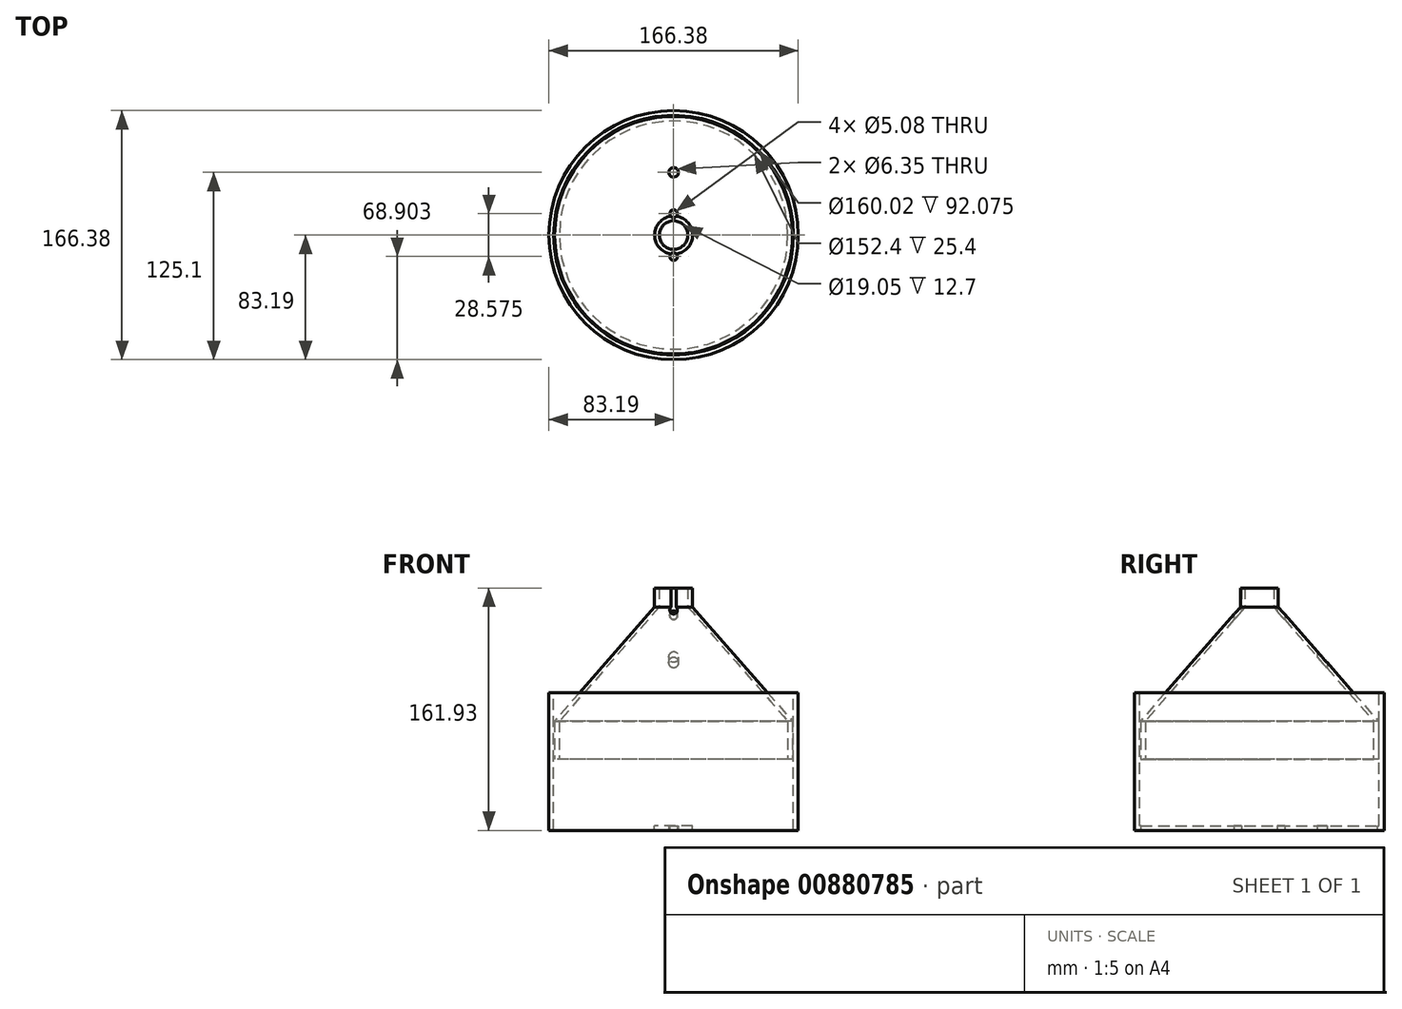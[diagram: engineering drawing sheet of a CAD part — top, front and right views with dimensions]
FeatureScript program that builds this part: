
annotation { "Feature Type Name" : "Feature", "Feature Type Description" : "" }
export const myFeature = defineFeature(function(context is Context, id is Id, definition is map)
    precondition{}
    {
        {
            var Q0;
            Q0=qCreatedBy(makeId("Top.planeOp"),FACE);
            var sketch = newSketch(context, id + "F0", { "sketchPlane" : qUnion([Q0])});
            skCircle(sketch, "E0", {"center": v(0, 0) * mm, "radius": 76.2 * mm});
            skCircle(sketch, "E1", {"center": v(0, 0) * mm, "radius": 79.38 * mm});
            skSolve(sketch);
        }
        {
            var Q0;
            Q0=makeQuery(id+"F0.imprint","IMPRINT",FACE,{"disambiguationData":[TD([[makeQuery(id+"F0.imprint","IMPRINT",EDGE,{"derivedFrom":sQuery(id+"F0.wireOp",EDGE,"E0")}),-1.0]])]});
            extrude(context, id + "F1", {"entities" : qUnion([Q0]), "depth" : 25.4 * mm, "offsetDistance" : 25.4 * mm});
        }
        {
            var Q0;
            Q0=qCreatedBy(makeId("Top.planeOp"),FACE);
            cPlane(context, id + "F2", {"entities" : qUnion([Q0]), "cplaneType" : CPlaneType.OFFSET, "offset" : 101.6 * mm, "width" : 152.4 * mm, "height" : 152.4 * mm});
        }
        {
            var Q0;
            Q0=qCreatedBy(id+"F2.planeOp",FACE);
            var sketch = newSketch(context, id + "F3", { "sketchPlane" : qUnion([Q0])});
            skCircle(sketch, "E2", {"center": v(0, 0) * mm, "radius": 12.7 * mm});
            skCircle(sketch, "E3", {"center": v(0, 0) * mm, "radius": 9.53 * mm, "construction": true});
            skSolve(sketch);
        }
        {
            var Q0;
            Q0=makeQuery(id+"F1.opExtrude","CAP_FACE",FACE,{"disambiguationData":[OSD([sQuery(id+"F0.wireOp",EDGE,"E0"),sQuery(id+"F0.wireOp",EDGE,"E1")])],"isStart":false});
            var sketch = newSketch(context, id + "F4", { "sketchPlane" : qUnion([Q0])});
            skCircle(sketch, "E4.0", {"center": v(0, 0) * mm, "radius": 79.38 * mm});
            skSolve(sketch);
        }
        {
            var Q1;
            Q1 = qSketchRegion(id + "F4", true);
            var Q2;
            Q2=makeQuery(id+"F3.imprint","IMPRINT",FACE,{"disambiguationData":[TD([[makeQuery(id+"F3.imprint","IMPRINT",EDGE,{"derivedFrom":sQuery(id+"F3.wireOp",EDGE,"E2")}),1.0]])]});
            loft(context, id + "F5", {"operationType" : NewBodyOperationType.ADD, "sheetProfilesArray" : [{ "sheetProfileEntities" : qUnion([Q1]) }, { "sheetProfileEntities" : qUnion([Q2]) }]});
        }
        {
            var Q0;
            Q0=makeQuery(id+"F5.opLoft","CAP_FACE",FACE,{"disambiguationData":[OSD([makeQuery(id+"F4.imprint","IMPRINT",FACE,{"disambiguationData":[TD([[makeQuery(id+"F4.imprint","IMPRINT",EDGE,{"derivedFrom":makeQuery(id+"F1.opExtrude","CAP_EDGE",EDGE,{"disambiguationData":[OSD([sQuery(id+"F0.wireOp",EDGE,"E0")])],"isStart":false})}),1.0]])]})])],"isStart":true});
            var sketch = newSketch(context, id + "F6", { "sketchPlane" : qUnion([Q0])});
            skCircle(sketch, "E5.0", {"center": v(0, 0) * mm, "radius": 76.2 * mm});
            skSolve(sketch);
        }
        {
            var Q0;
            Q0=makeQuery(id+"F3.imprint","IMPRINT",FACE,{"disambiguationData":[TD([[makeQuery(id+"F3.imprint","IMPRINT",EDGE,{"derivedFrom":sQuery(id+"F3.wireOp",EDGE,"E2")}),1.0]])]});
            var sketch = newSketch(context, id + "F7", { "sketchPlane" : qUnion([Q0])});
            skCircle(sketch, "E6", {"center": v(0, 0) * mm, "radius": 9.53 * mm});
            skSolve(sketch);
        }
        {
            var Q1;
            Q1 = qSketchRegion(id + "F7", true);
            var Q2;
            Q2 = qSketchRegion(id + "F6", true);
            loft(context, id + "F8", {"operationType" : NewBodyOperationType.REMOVE, "sheetProfilesArray" : [{ "sheetProfileEntities" : qUnion([Q1]) }, { "sheetProfileEntities" : qUnion([Q2]) }]});
        }
        {
            var Q0;
            Q0=makeQuery(id+"F3.imprint","IMPRINT",FACE,{"disambiguationData":[TD([[makeQuery(id+"F3.imprint","IMPRINT",EDGE,{"derivedFrom":sQuery(id+"F3.wireOp",EDGE,"E2")}),1.0]])]});
            var sketch = newSketch(context, id + "F9", { "sketchPlane" : qUnion([Q0])});
            skCircle(sketch, "E7.0.0", {"center": v(0, 0) * mm, "radius": 12.7 * mm});
            skCircle(sketch, "E8.0", {"center": v(0, 0) * mm, "radius": 9.53 * mm});
            skSolve(sketch);
        }
        {
            var Q0;
            Q0 = qSketchRegion(id + "F9", true);
            extrude(context, id + "F10", {"entities" : qUnion([Q0]), "operationType" : NewBodyOperationType.ADD, "depth" : 12.7 * mm, "offsetDistance" : 25.4 * mm});
        }
        {
            var Q0;
            Q0=makeQuery(id+"F1.opExtrude","CAP_FACE",FACE,{"disambiguationData":[OSD([sQuery(id+"F0.wireOp",EDGE,"E0"),sQuery(id+"F0.wireOp",EDGE,"E1")])],"isStart":true});
            var sketch = newSketch(context, id + "F11", { "sketchPlane" : qUnion([Q0])});
            skCircle(sketch, "E9.0", {"center": v(0, 0) * mm, "radius": 83.19 * mm});
            skCircle(sketch, "E10", {"center": v(0, 0) * mm, "radius": 80.01 * mm});
            skSolve(sketch);
        }
        {
            var Q0;
            Q0 = qSketchRegion(id + "F11", true);
            extrude(context, id + "F12", {"entities" : qUnion([Q0]), "endBound" : BoundingType.SYMMETRIC, "depth" : 88.9 * mm, "offsetDistance" : 25.4 * mm});
        }
        {
            var Q0;
            Q0=makeQuery(id+"F12.opExtrude","CAP_FACE",FACE,{"disambiguationData":[OSD([sQuery(id+"F11.wireOp",EDGE,"E9.0"),sQuery(id+"F11.wireOp",EDGE,"E10")])],"isStart":false});
            var sketch = newSketch(context, id + "F13", { "sketchPlane" : qUnion([Q0])});
            skLineSegment(sketch, "E11", {"start": v(0, 80.01) * mm, "end": v(0, -80.01) * mm, "construction": true});
            skLineSegment(sketch, "E12", {"start": v(-12.7, 79) * mm, "end": v(-12.7, -79) * mm});
            skLineSegment(sketch, "E13", {"start": v(12.7, 79) * mm, "end": v(12.7, -79) * mm});
            skLineSegment(sketch, "E14", {"start": v(-12.7, 104.4) * mm, "end": v(12.7, 104.4) * mm});
            skLineSegment(sketch, "E15", {"start": v(12.7, 104.4) * mm, "end": v(12.7, 79) * mm});
            skLineSegment(sketch, "E16", {"start": v(-12.7, 104.4) * mm, "end": v(-12.7, 79) * mm});
            skLineSegment(sketch, "E17", {"start": v(-12.7, -79) * mm, "end": v(-12.7, -104.4) * mm});
            skLineSegment(sketch, "E18", {"start": v(-12.7, -104.4) * mm, "end": v(12.7, -104.4) * mm});
            skLineSegment(sketch, "E19", {"start": v(12.7, -104.4) * mm, "end": v(12.7, -79) * mm});
            skSolve(sketch);
        }
        {
            var Q0;
            Q0 = qSketchRegion(id + "F13", true);
            extrude(context, id + "F14", {"entities" : qUnion([Q0]), "operationType" : NewBodyOperationType.ADD, "depth" : 3.17 * mm, "offsetDistance" : 25.4 * mm});
        }
        {
            var Q0;
            {var subQ0=sQuery(id+"F11.wireOp",EDGE,"E9.0");var subQ1=sQuery(id+"F13.wireOp",EDGE,"E17");var subQ2=sQuery(id+"F13.wireOp",EDGE,"E16");var subQ3=sQuery(id+"F13.wireOp",EDGE,"E12");var subQ4=sQuery(id+"F11.wireOp",EDGE,"E10");Q0=makeQuery(id+"F14.boolean.opBoolean","SPLIT",FACE,{"disambiguationData":[TD([makeQuery(id+"F14.opExtrude","SWEPT_FACE",FACE,{"disambiguationData":[OSD([subQ3,subQ2,subQ1])]})])],"derivedFrom":makeQuery(id+"F12.opExtrude","CAP_FACE",FACE,{"disambiguationData":[OSD([subQ0,subQ4])],"isStart":false})});}
            var sketch = newSketch(context, id + "F15", { "sketchPlane" : qUnion([Q0])});
            skCircle(sketch, "E20.0", {"center": v(0, 0) * mm, "radius": 83.19 * mm});
            skCircle(sketch, "E21", {"center": v(0, 0) * mm, "radius": 80.01 * mm});
            skSolve(sketch);
        }
        {
            var Q0;
            Q0 = qSketchRegion(id + "F15", true);
            extrude(context, id + "F16", {"entities" : qUnion([Q0]), "operationType" : NewBodyOperationType.ADD, "depth" : 3.17 * mm, "offsetDistance" : 25.4 * mm});
        }
        {
            var Q0;
            Q0=makeQuery(id+"F16.boolean.opBoolean","MERGE",FACE,{"derivedFrom":[makeQuery(id+"F14.opExtrude","CAP_FACE",FACE,{"disambiguationData":[OSD([sQuery(id+"F13.wireOp",EDGE,"E12"),sQuery(id+"F13.wireOp",EDGE,"E13"),sQuery(id+"F13.wireOp",EDGE,"E14"),sQuery(id+"F13.wireOp",EDGE,"E15"),sQuery(id+"F13.wireOp",EDGE,"E16"),sQuery(id+"F13.wireOp",EDGE,"E17"),sQuery(id+"F13.wireOp",EDGE,"E18"),sQuery(id+"F13.wireOp",EDGE,"E19")])],"isStart":false}),makeQuery(id+"F16.opExtrude","CAP_FACE",FACE,{"disambiguationData":[OSD([sQuery(id+"F15.wireOp",EDGE,"E20.0"),sQuery(id+"F15.wireOp",EDGE,"E21")])],"isStart":false})]});
            var sketch = newSketch(context, id + "F17", { "sketchPlane" : qUnion([Q0])});
            skCircle(sketch, "E22", {"center": v(0, 14.29) * mm, "radius": 2.54 * mm});
            skCircle(sketch, "E23", {"center": v(0, -14.29) * mm, "radius": 2.54 * mm});
            skCircle(sketch, "E24", {"center": v(0, -41.91) * mm, "radius": 3.18 * mm});
            skSolve(sketch);
        }
        {
            var Q0;
            Q0 = qSketchRegion(id + "F17", true);
            extrude(context, id + "F18", {"entities" : qUnion([Q0]), "operationType" : NewBodyOperationType.REMOVE, "endBound" : BoundingType.THROUGH_ALL, "oppositeDirection" : true, "depth" : 25.4 * mm, "offsetDistance" : 25.4 * mm});
        }
        {
            var Q0;
            Q0=makeQuery(id+"F16.boolean.opBoolean","MERGE",FACE,{"derivedFrom":[makeQuery(id+"F14.opExtrude","CAP_FACE",FACE,{"disambiguationData":[OSD([sQuery(id+"F13.wireOp",EDGE,"E12"),sQuery(id+"F13.wireOp",EDGE,"E13"),sQuery(id+"F13.wireOp",EDGE,"E14"),sQuery(id+"F13.wireOp",EDGE,"E15"),sQuery(id+"F13.wireOp",EDGE,"E16"),sQuery(id+"F13.wireOp",EDGE,"E17"),sQuery(id+"F13.wireOp",EDGE,"E18"),sQuery(id+"F13.wireOp",EDGE,"E19")])],"isStart":false}),makeQuery(id+"F16.opExtrude","CAP_FACE",FACE,{"disambiguationData":[OSD([sQuery(id+"F15.wireOp",EDGE,"E20.0"),sQuery(id+"F15.wireOp",EDGE,"E21")])],"isStart":false})]});
            var sketch = newSketch(context, id + "F19", { "sketchPlane" : qUnion([Q0])});
            skLineSegment(sketch, "E25.0", {"start": v(-12.7, 104.4) * mm, "end": v(-12.7, 82.2) * mm});
            skLineSegment(sketch, "E25.1", {"start": v(-12.7, 104.4) * mm, "end": v(12.7, 104.4) * mm});
            skLineSegment(sketch, "E25.2", {"start": v(12.7, 104.4) * mm, "end": v(12.7, 82.2) * mm});
            skArc(sketch, "E26.0", {"start": v(-12.7, -82.2) * mm, "mid": v(0, -83.18) * mm, "end": v(12.7, -82.2) * mm});
            skLineSegment(sketch, "E27.0", {"start": v(-12.7, -82.2) * mm, "end": v(-12.7, -104.4) * mm});
            skLineSegment(sketch, "E28.0", {"start": v(-12.7, -104.4) * mm, "end": v(12.7, -104.4) * mm});
            skLineSegment(sketch, "E29.0", {"start": v(12.7, -82.2) * mm, "end": v(12.7, -104.4) * mm});
            skArc(sketch, "E30.trimOffspring", {"start": v(12.7, 82.2) * mm, "mid": v(0, 83.19) * mm, "end": v(-12.7, 82.2) * mm});
            skSolve(sketch);
        }
        {
            var Q0;
            Q0 = qSketchRegion(id + "F19", true);
            extrude(context, id + "F20", {"entities" : qUnion([Q0]), "operationType" : NewBodyOperationType.REMOVE, "oppositeDirection" : true, "depth" : 25.4 * mm, "offsetDistance" : 25.4 * mm});
        }
    });
